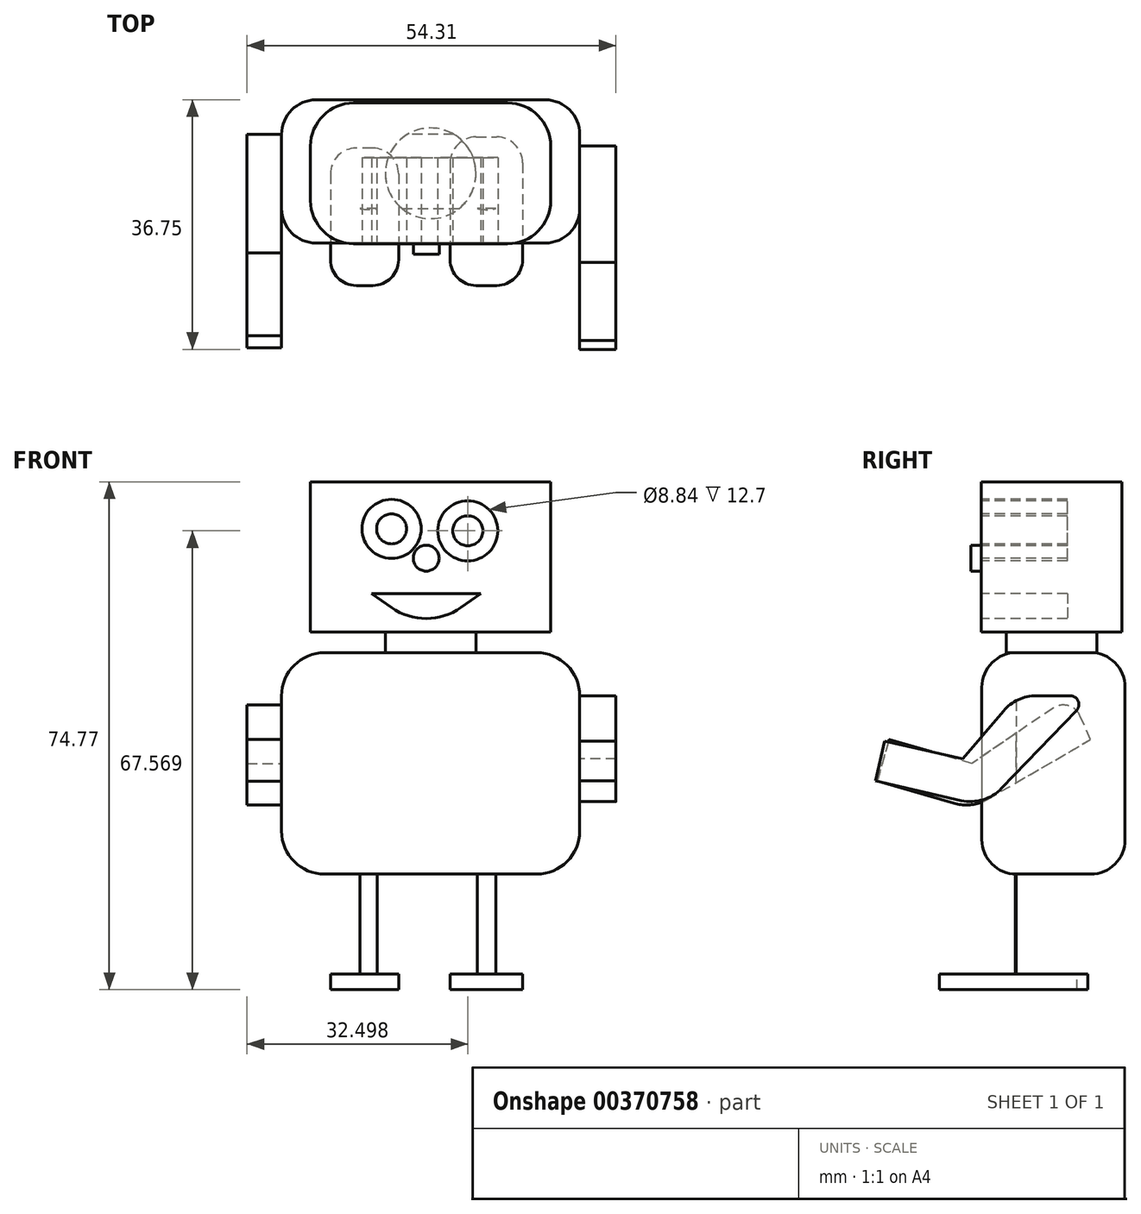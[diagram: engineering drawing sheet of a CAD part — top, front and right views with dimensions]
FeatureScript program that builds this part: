
annotation { "Feature Type Name" : "Feature", "Feature Type Description" : "" }
export const myFeature = defineFeature(function(context is Context, id is Id, definition is map)
    precondition{}
    {
        {
            var Q0;
            Q0=qCreatedBy(makeId("Front.planeOp"),FACE);
            var sketch = newSketch(context, id + "F0", { "sketchPlane" : qUnion([Q0])});
            skLineSegment(sketch, "E0.bottom", {"start": v(15.6, 16.3) * mm, "end": v(-15.6, 16.3) * mm});
            skLineSegment(sketch, "E0.top", {"start": v(15.6, -16.3) * mm, "end": v(-15.6, -16.3) * mm});
            skLineSegment(sketch, "E0.left", {"start": v(21.95, 9.96) * mm, "end": v(21.95, -9.96) * mm});
            skLineSegment(sketch, "E0.right", {"start": v(-21.95, 9.96) * mm, "end": v(-21.95, -9.96) * mm});
            skPoint(sketch, "E0.middle", {"position": v(0, 0) * mm});
            skPoint(sketch, "E1.visualSharp", {"position": v(-21.95, 16.3) * mm});
            skArc(sketch, "E1.filletArc", {"start": v(-15.6, 16.3) * mm, "mid": v(-20.09, 14.45) * mm, "end": v(-21.95, 9.96) * mm});
            skPoint(sketch, "E2.visualSharp", {"position": v(21.95, 16.3) * mm});
            skArc(sketch, "E2.filletArc", {"start": v(21.95, 9.96) * mm, "mid": v(20.09, 14.45) * mm, "end": v(15.6, 16.3) * mm});
            skPoint(sketch, "E3.visualSharp", {"position": v(-21.95, -16.3) * mm});
            skArc(sketch, "E3.filletArc", {"start": v(-21.95, -9.96) * mm, "mid": v(-20.09, -14.45) * mm, "end": v(-15.6, -16.3) * mm});
            skPoint(sketch, "E4.visualSharp", {"position": v(21.95, -16.3) * mm});
            skArc(sketch, "E4.filletArc", {"start": v(15.6, -16.3) * mm, "mid": v(20.09, -14.45) * mm, "end": v(21.95, -9.96) * mm});
            skSolve(sketch);
        }
        {
            var Q0;
            Q0 = qSketchRegion(id + "F0", true);
            extrude(context, id + "F1", {"entities" : qUnion([Q0]), "depth" : 21.08 * mm});
        }
        {
            var Q0;
            Q0=makeQuery(id+"F1.opExtrude","SWEPT_FACE",FACE,{"disambiguationData":[OSD([sQuery(id+"F0.wireOp",EDGE,"E2.filletArc")])]});
            var Q1;
            Q1=makeQuery(id+"F1.opExtrude","SWEPT_FACE",FACE,{"disambiguationData":[OSD([sQuery(id+"F0.wireOp",EDGE,"E4.filletArc")])]});
            fillet(context, id + "F2", {"entities" : qUnion([Q0, Q1]), "radius" : 5.08 * mm, "tangentPropagation" : true, "allowEdgeOverflow" : false});
        }
        {
            var Q0;
            Q0=makeQuery(id+"F1.opExtrude","SWEPT_FACE",FACE,{"disambiguationData":[OSD([sQuery(id+"F0.wireOp",EDGE,"E0.bottom")])]});
            var sketch = newSketch(context, id + "F3", { "sketchPlane" : qUnion([Q0])});
            skCircle(sketch, "E5", {"center": v(0, -10.82) * mm, "radius": 6.67 * mm});
            skSolve(sketch);
        }
        {
            var Q0;
            Q0 = qSketchRegion(id + "F3", true);
            extrude(context, id + "F4", {"entities" : qUnion([Q0]), "operationType" : NewBodyOperationType.ADD, "depth" : 3.05 * mm});
        }
        {
            var Q0;
            Q0=makeQuery(id+"F1.opExtrude","SWEPT_FACE",FACE,{"disambiguationData":[OSD([sQuery(id+"F0.wireOp",EDGE,"E0.top")])]});
            var sketch = newSketch(context, id + "F5", { "sketchPlane" : qUnion([Q0])});
            skPoint(sketch, "E6.endSnap0", {"position": v(-15.6, 10.54) * mm});
            skCircle(sketch, "E7", {"center": v(-9.14, 10.54) * mm, "radius": 5.6 * mm});
            skCircle(sketch, "E8", {"center": v(8.23, 10.54) * mm, "radius": 5.62 * mm});
            skSolve(sketch);
        }
        {
            var Q0;
            {var subQ0=sQuery(id+"F5.wireOp",EDGE,"E7");var subQ1=sQuery(id+"F0.wireOp",EDGE,"E0.top");var subQ2=makeQuery(id+"F1.opExtrude","SWEPT_FACE",FACE,{"disambiguationData":[OSD([subQ1])]});var subQ3=makeQuery(id+"F2.opFillet","BLEND_EDGE",EDGE,{"blendedFrom":[makeQuery(id+"F1.opExtrude","CAP_EDGE",EDGE,{"disambiguationData":[OSD([subQ1])],"isStart":false}),subQ2],"blendedInto":[subQ2]});var subQ4=makeQuery(id+"F5.imprint","INTERSECT",VERTEX,{"disambiguationData":[OD(0.0)],"derivedFrom":[subQ3,subQ0]});Q0=makeQuery(id+"F5.imprint","IMPRINT",FACE,{"disambiguationData":[TD([[makeQuery(id+"F5.imprint","IMPRINT",EDGE,{"disambiguationData":[TD([[subQ4,-1.0]])],"derivedFrom":subQ0}),1.0]])]});}
            var Q1;
            {var subQ0=sQuery(id+"F5.wireOp",EDGE,"E8");var subQ1=sQuery(id+"F0.wireOp",EDGE,"E0.top");var subQ2=makeQuery(id+"F1.opExtrude","SWEPT_FACE",FACE,{"disambiguationData":[OSD([subQ1])]});var subQ3=makeQuery(id+"F2.opFillet","BLEND_EDGE",EDGE,{"blendedFrom":[makeQuery(id+"F1.opExtrude","CAP_EDGE",EDGE,{"disambiguationData":[OSD([subQ1])],"isStart":false}),subQ2],"blendedInto":[subQ2]});var subQ4=makeQuery(id+"F5.imprint","INTERSECT",VERTEX,{"disambiguationData":[OD(0.0)],"derivedFrom":[subQ3,subQ0]});Q1=makeQuery(id+"F5.imprint","IMPRINT",FACE,{"disambiguationData":[TD([[makeQuery(id+"F5.imprint","IMPRINT",EDGE,{"disambiguationData":[TD([[subQ4,-1.0]])],"derivedFrom":subQ0}),1.0]])]});}
            extrude(context, id + "F6", {"entities" : qUnion([Q0, Q1]), "operationType" : NewBodyOperationType.ADD, "depth" : 14.73 * mm});
        }
        {
            var Q0;
            Q0=makeQuery(id+"F4.opExtrude","CAP_FACE",FACE,{"disambiguationData":[OSD([sQuery(id+"F3.wireOp",EDGE,"E5")])],"isStart":false});
            var sketch = newSketch(context, id + "F7", { "sketchPlane" : qUnion([Q0])});
            skLineSegment(sketch, "E9.bottom", {"start": v(11.33, -21.18) * mm, "end": v(-11.33, -21.18) * mm});
            skLineSegment(sketch, "E9.top", {"start": v(11.33, -0.46) * mm, "end": v(-11.33, -0.46) * mm});
            skLineSegment(sketch, "E9.left", {"start": v(17.68, -14.83) * mm, "end": v(17.68, -6.8) * mm});
            skLineSegment(sketch, "E9.right", {"start": v(-17.68, -14.83) * mm, "end": v(-17.68, -6.8) * mm});
            skPoint(sketch, "E9.middle", {"position": v(0, -10.82) * mm});
            skPoint(sketch, "E10.visualSharp", {"position": v(17.68, -0.46) * mm});
            skArc(sketch, "E10.filletArc", {"start": v(17.68, -6.8) * mm, "mid": v(15.82, -2.32) * mm, "end": v(11.33, -0.46) * mm});
            skPoint(sketch, "E11.visualSharp", {"position": v(-17.68, -0.46) * mm});
            skArc(sketch, "E11.filletArc", {"start": v(-11.33, -0.46) * mm, "mid": v(-15.82, -2.32) * mm, "end": v(-17.68, -6.8) * mm});
            skPoint(sketch, "E12.visualSharp", {"position": v(-17.68, -21.18) * mm});
            skArc(sketch, "E12.filletArc", {"start": v(-17.68, -14.83) * mm, "mid": v(-15.82, -19.32) * mm, "end": v(-11.33, -21.18) * mm});
            skPoint(sketch, "E13.visualSharp", {"position": v(17.68, -21.18) * mm});
            skArc(sketch, "E13.filletArc", {"start": v(11.33, -21.18) * mm, "mid": v(15.82, -19.32) * mm, "end": v(17.68, -14.83) * mm});
            skSolve(sketch);
        }
        {
            var Q0;
            Q0 = qSketchRegion(id + "F7", true);
            extrude(context, id + "F8", {"entities" : qUnion([Q0]), "operationType" : NewBodyOperationType.ADD, "depth" : 22.1 * mm});
        }
        {
            var Q0;
            Q0=makeQuery(id+"F1.opExtrude","SWEPT_FACE",FACE,{"disambiguationData":[OSD([sQuery(id+"F0.wireOp",EDGE,"E0.left")])]});
            var sketch = newSketch(context, id + "F9", { "sketchPlane" : qUnion([Q0])});
            skLineSegment(sketch, "E14", {"start": v(-7.16, 7.8) * mm, "end": v(-18.17, -3.66) * mm});
            skLineSegment(sketch, "E15", {"start": v(-24.15, -5.45) * mm, "end": v(-36.75, -2.6) * mm});
            skLineSegment(sketch, "E16", {"start": v(-36.75, -2.6) * mm, "end": v(-35.42, 3.28) * mm});
            skLineSegment(sketch, "E17", {"start": v(-35.42, 3.28) * mm, "end": v(-23.93, 0.68) * mm});
            skLineSegment(sketch, "E18", {"start": v(-23.93, 0.68) * mm, "end": v(-17.9, 7.73) * mm});
            skLineSegment(sketch, "E19", {"start": v(-13.07, 9.96) * mm, "end": v(-8.08, 9.96) * mm});
            skPoint(sketch, "E20.visualSharp", {"position": v(-16, 9.96) * mm});
            skArc(sketch, "E20.filletArc", {"start": v(-13.07, 9.96) * mm, "mid": v(-15.73, 9.37) * mm, "end": v(-17.9, 7.73) * mm});
            skPoint(sketch, "E21.visualSharp", {"position": v(-20.65, -6.25) * mm});
            skArc(sketch, "E21.filletArc", {"start": v(-24.15, -5.45) * mm, "mid": v(-20.92, -5.34) * mm, "end": v(-18.17, -3.66) * mm});
            skPoint(sketch, "E22.visualSharp", {"position": v(-5.08, 9.96) * mm});
            skArc(sketch, "E22.filletArc", {"start": v(-7.16, 7.8) * mm, "mid": v(-6.9, 9.18) * mm, "end": v(-8.08, 9.96) * mm});
            skSolve(sketch);
        }
        {
            var Q0;
            Q0 = qSketchRegion(id + "F9", true);
            extrude(context, id + "F10", {"entities" : qUnion([Q0]), "operationType" : NewBodyOperationType.ADD, "depth" : 5.33 * mm});
        }
        {
            var Q0;
            Q0=makeQuery(id+"F1.opExtrude","SWEPT_FACE",FACE,{"disambiguationData":[OSD([sQuery(id+"F0.wireOp",EDGE,"E0.right")])]});
            var sketch = newSketch(context, id + "F11", { "sketchPlane" : qUnion([Q0])});
            skLineSegment(sketch, "E23", {"start": v(7.92, 9.96) * mm, "end": v(22.56, 0) * mm});
            skLineSegment(sketch, "E24", {"start": v(22.56, 0) * mm, "end": v(34.75, 3.5) * mm});
            skLineSegment(sketch, "E25", {"start": v(34.75, 3.5) * mm, "end": v(36.5, -2.61) * mm});
            skLineSegment(sketch, "E26", {"start": v(36.5, -2.61) * mm, "end": v(25.15, -5.87) * mm});
            skLineSegment(sketch, "E27", {"start": v(20.22, -5.27) * mm, "end": v(5.08, 3.5) * mm});
            skLineSegment(sketch, "E28", {"start": v(5.08, 3.5) * mm, "end": v(7.92, 9.96) * mm});
            skPoint(sketch, "E29.visualSharp", {"position": v(22.56, -6.62) * mm});
            skArc(sketch, "E29.filletArc", {"start": v(20.22, -5.27) * mm, "mid": v(22.62, -6.07) * mm, "end": v(25.15, -5.87) * mm});
            skSolve(sketch);
        }
        {
            var Q0;
            Q0 = qSketchRegion(id + "F11", true);
            extrude(context, id + "F12", {"entities" : qUnion([Q0]), "operationType" : NewBodyOperationType.ADD, "depth" : 5.08 * mm});
        }
        {
            var Q0;
            Q0=makeQuery(id+"F8.opExtrude","SWEPT_FACE",FACE,{"disambiguationData":[OSD([sQuery(id+"F7.wireOp",EDGE,"E9.bottom")])]});
            var sketch = newSketch(context, id + "F13", { "sketchPlane" : qUnion([Q0])});
            skLineSegment(sketch, "E30", {"start": v(-8.71, 25) * mm, "end": v(7.4, 25) * mm});
            skLineSegment(sketch, "E31", {"start": v(-8.71, 25) * mm, "end": v(-5.76, 22.94) * mm});
            skPoint(sketch, "E31.endSnap0", {"position": v(-0.65, 25) * mm});
            skLineSegment(sketch, "E32", {"start": v(4.45, 22.94) * mm, "end": v(7.4, 25) * mm});
            skPoint(sketch, "E33.visualSharp", {"position": v(-0.65, 19.35) * mm});
            skArc(sketch, "E33.filletArc", {"start": v(-5.76, 22.94) * mm, "mid": v(-0.65, 21.33) * mm, "end": v(4.45, 22.94) * mm});
            skCircle(sketch, "E34", {"center": v(5.47, 34.25) * mm, "radius": 4.42 * mm});
            skCircle(sketch, "E35", {"center": v(-5.75, 34.53) * mm, "radius": 4.35 * mm});
            skCircle(sketch, "E36", {"center": v(-5.75, 34.53) * mm, "radius": 2.2 * mm});
            skCircle(sketch, "E37", {"center": v(5.47, 34.25) * mm, "radius": 2.2 * mm});
            skSolve(sketch);
        }
        {
            var Q0;
            Q0 = qSketchRegion(id + "F13", true);
            extrude(context, id + "F14", {"entities" : qUnion([Q0]), "operationType" : NewBodyOperationType.REMOVE, "oppositeDirection" : true, "depth" : 12.7 * mm});
        }
        {
            var Q0;
            Q0=makeQuery(id+"F12.opExtrude","SWEPT_EDGE",EDGE,{"disambiguationData":[OSD([sQuery(id+"F0.wireOp",EDGE,"E0.right"),sQuery(id+"F0.wireOp",EDGE,"E1.filletArc"),sQuery(id+"F11.wireOp",EDGE,"E23"),sQuery(id+"F11.wireOp",EDGE,"E28")])]});
            fillet(context, id + "F15", {"entities" : qUnion([Q0]), "radius" : 2.7 * mm, "tangentPropagation" : true, "allowEdgeOverflow" : false});
        }
        {
            var Q0;
            {var subQ1=sQuery(id+"F7.wireOp",EDGE,"E12.filletArc");var subQ7=sQuery(id+"F7.wireOp",EDGE,"E9.bottom");Q0=makeQuery(id+"F14.boolean.opBoolean","SPLIT",FACE,{"disambiguationData":[TD([makeQuery(id+"F8.opExtrude","SWEPT_FACE",FACE,{"disambiguationData":[OSD([subQ1])]})])],"derivedFrom":makeQuery(id+"F8.opExtrude","SWEPT_FACE",FACE,{"disambiguationData":[OSD([subQ7])]})});}
            var sketch = newSketch(context, id + "F16", { "sketchPlane" : qUnion([Q0])});
            skCircle(sketch, "E38", {"center": v(-0.65, 30.22) * mm, "radius": 1.9 * mm});
            skSolve(sketch);
        }
        {
            var Q0;
            Q0 = qSketchRegion(id + "F16", true);
            extrude(context, id + "F17", {"entities" : qUnion([Q0]), "operationType" : NewBodyOperationType.ADD, "depth" : 1.52 * mm});
        }
        {
            var Q0;
            Q0=makeQuery(id+"F6.opExtrude","CAP_FACE",FACE,{"disambiguationData":[OSD([sQuery(id+"F0.wireOp",EDGE,"E0.top"),sQuery(id+"F5.wireOp",EDGE,"E7")])],"isStart":false});
            var sketch = newSketch(context, id + "F18", { "sketchPlane" : qUnion([Q0])});
            skLineSegment(sketch, "E39.bottom", {"start": v(6.69, 5.47) * mm, "end": v(9.72, 5.47) * mm});
            skLineSegment(sketch, "E39.top", {"start": v(6.69, 27.34) * mm, "end": v(9.72, 27.34) * mm});
            skLineSegment(sketch, "E39.left", {"start": v(2.88, 9.28) * mm, "end": v(2.88, 23.53) * mm});
            skLineSegment(sketch, "E39.right", {"start": v(13.53, 9.28) * mm, "end": v(13.53, 23.53) * mm});
            skLineSegment(sketch, "E40.bottom", {"start": v(-8.53, 7.1) * mm, "end": v(-10.94, 7.1) * mm});
            skLineSegment(sketch, "E40.top", {"start": v(-8.53, 27.34) * mm, "end": v(-10.94, 27.34) * mm});
            skLineSegment(sketch, "E40.left", {"start": v(-4.72, 10.9) * mm, "end": v(-4.72, 23.53) * mm});
            skLineSegment(sketch, "E40.right", {"start": v(-14.75, 10.9) * mm, "end": v(-14.75, 23.53) * mm});
            skPoint(sketch, "E41.visualSharp", {"position": v(13.53, 5.47) * mm});
            skArc(sketch, "E41.filletArc", {"start": v(9.72, 5.47) * mm, "mid": v(12.41, 6.58) * mm, "end": v(13.53, 9.28) * mm});
            skPoint(sketch, "E42.visualSharp", {"position": v(2.88, 5.47) * mm});
            skArc(sketch, "E42.filletArc", {"start": v(2.88, 9.28) * mm, "mid": v(4, 6.58) * mm, "end": v(6.69, 5.47) * mm});
            skPoint(sketch, "E43.visualSharp", {"position": v(13.53, 27.34) * mm});
            skArc(sketch, "E43.filletArc", {"start": v(13.53, 23.53) * mm, "mid": v(12.41, 26.23) * mm, "end": v(9.72, 27.34) * mm});
            skPoint(sketch, "E44.visualSharp", {"position": v(2.88, 27.34) * mm});
            skArc(sketch, "E44.filletArc", {"start": v(6.69, 27.34) * mm, "mid": v(4, 26.23) * mm, "end": v(2.88, 23.53) * mm});
            skPoint(sketch, "E45.visualSharp", {"position": v(-4.72, 27.34) * mm});
            skArc(sketch, "E45.filletArc", {"start": v(-4.72, 23.53) * mm, "mid": v(-5.83, 26.23) * mm, "end": v(-8.53, 27.34) * mm});
            skPoint(sketch, "E46.visualSharp", {"position": v(-14.75, 27.34) * mm});
            skArc(sketch, "E46.filletArc", {"start": v(-10.94, 27.34) * mm, "mid": v(-13.64, 26.23) * mm, "end": v(-14.75, 23.53) * mm});
            skPoint(sketch, "E47.visualSharp", {"position": v(-14.75, 7.1) * mm});
            skArc(sketch, "E47.filletArc", {"start": v(-14.75, 10.9) * mm, "mid": v(-13.64, 8.21) * mm, "end": v(-10.94, 7.1) * mm});
            skPoint(sketch, "E48.visualSharp", {"position": v(-4.72, 7.1) * mm});
            skArc(sketch, "E48.filletArc", {"start": v(-8.53, 7.1) * mm, "mid": v(-5.83, 8.21) * mm, "end": v(-4.72, 10.9) * mm});
            skSolve(sketch);
        }
        {
            var Q0;
            Q0 = qSketchRegion(id + "F18", true);
            extrude(context, id + "F19", {"entities" : qUnion([Q0]), "operationType" : NewBodyOperationType.ADD, "flatOperationType" : FlatOperationType.REMOVE, "offsetDistance" : 25.4 * mm, "depth" : 2.3 * mm, "domain" : OperationDomain.MODEL});
        }
    });
